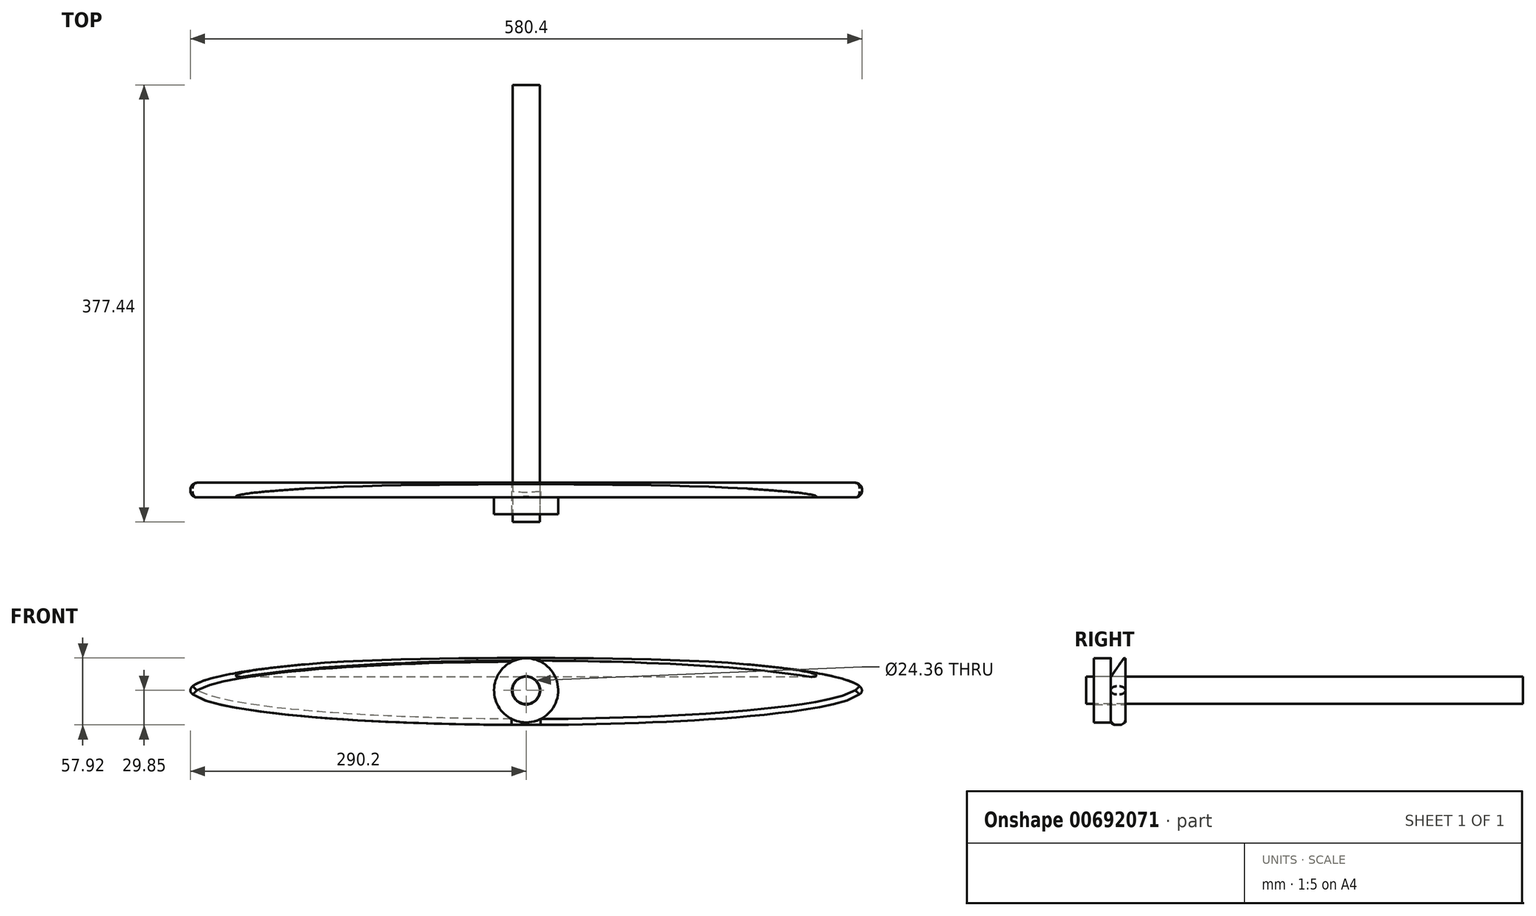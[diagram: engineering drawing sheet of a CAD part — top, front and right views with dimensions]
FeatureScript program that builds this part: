
annotation { "Feature Type Name" : "Feature", "Feature Type Description" : "" }
export const myFeature = defineFeature(function(context is Context, id is Id, definition is map)
    precondition{}
    {
        {
            var Q0;
            Q0=qCreatedBy(makeId("Front.planeOp"),FACE);
            var sketch = newSketch(context, id + "F0", { "sketchPlane" : qUnion([Q0])});
            skEllipse(sketch, "E0", {"center": v(0, 0) * mm, "majorRadius": 290.2 * mm, "minorRadius": 29.85 * mm, "majorAxis": v(1, 0)});
            skCircle(sketch, "E1", {"center": v(0, 0) * mm, "radius": 27.71 * mm});
            skCircle(sketch, "E2", {"center": v(0, 0) * mm, "radius": 12.18 * mm});
            skSolve(sketch);
        }
        {
            var Q0;
            Q0=makeQuery(id+"F0.imprint","IMPRINT",FACE,{"disambiguationData":[TD([[makeQuery(id+"F0.imprint","IMPRINT",EDGE,{"derivedFrom":sQuery(id+"F0.wireOp",EDGE,"E0")}),1.0]])]});
            extrude(context, id + "F1", {"entities" : qUnion([Q0]), "endBound" : BoundingType.SYMMETRIC, "oppositeDirection" : true, "depth" : 12.7 * mm, "offsetDistance" : 25.4 * mm});
        }
        {
            var Q0;
            Q0=makeQuery(id+"F0.imprint","IMPRINT",FACE,{"disambiguationData":[TD([[makeQuery(id+"F0.imprint","IMPRINT",EDGE,{"derivedFrom":sQuery(id+"F0.wireOp",EDGE,"E1")}),1.0]])]});
            extrude(context, id + "F2", {"entities" : qUnion([Q0]), "operationType" : NewBodyOperationType.ADD, "depth" : 20.83 * mm, "offsetDistance" : 25.4 * mm});
        }
        {
            var Q0;
            Q0=makeQuery(id+"F1.opExtrude","CAP_EDGE",EDGE,{"disambiguationData":[OSD([sQuery(id+"F0.wireOp",EDGE,"E0")])],"isStart":true});
            var Q1;
            Q1=makeQuery(id+"F1.opExtrude","CAP_EDGE",EDGE,{"disambiguationData":[OSD([sQuery(id+"F0.wireOp",EDGE,"E0")])],"isStart":false});
            fillet(context, id + "F3", {"entities" : qUnion([Q0, Q1]), "radius" : 5.08 * mm, "tangentPropagation" : true, "allowEdgeOverflow" : false});
        }
        {
            var Q0;
            Q0=makeQuery(id+"F0.imprint","IMPRINT",FACE,{"disambiguationData":[TD([[makeQuery(id+"F0.imprint","IMPRINT",EDGE,{"derivedFrom":sQuery(id+"F0.wireOp",EDGE,"E1")}),1.0]])]});
            extrude(context, id + "F4", {"entities" : qUnion([Q0]), "operationType" : NewBodyOperationType.ADD, "oppositeDirection" : true, "depth" : 6.35 * mm, "offsetDistance" : 25.4 * mm});
        }
        {
            var Q0;
            Q0=qCreatedBy(makeId("Right.planeOp"),FACE);
            var sketch = newSketch(context, id + "F5", { "sketchPlane" : qUnion([Q0])});
            skLineSegment(sketch, "E3", {"start": v(18.47, 47.35) * mm, "end": v(-6.25, 11.6) * mm});
            skLineSegment(sketch, "E4", {"start": v(-6.25, 11.6) * mm, "end": v(-6.25, 33.84) * mm});
            skLineSegment(sketch, "E5", {"start": v(-6.25, 33.84) * mm, "end": v(18.47, 47.35) * mm});
            skSolve(sketch);
        }
        {
            var Q0;
            Q0 = qSketchRegion(id + "F5", true);
            extrude(context, id + "F6", {"entities" : qUnion([Q0]), "operationType" : NewBodyOperationType.REMOVE, "endBound" : BoundingType.SYMMETRIC, "depth" : 772.16 * mm, "offsetDistance" : 25.4 * mm});
        }
        {
            var Q0;
            Q0=sQuery(id+"F0.wireOp",EDGE,"E1");
            extrude(context, id + "F7", {"bodyType" : ToolBodyType.SURFACE, "surfaceEntities" : qUnion([Q0]), "oppositeDirection" : true, "depth" : 5.84 * mm, "offsetDistance" : 25.4 * mm});
        }
        {
            var Q0;
            Q0=qCreatedBy(makeId("Front.planeOp"),FACE);
            var sketch = newSketch(context, id + "F8", { "sketchPlane" : qUnion([Q0])});
            skCircle(sketch, "E6", {"center": v(0, 0) * mm, "radius": 11.77 * mm});
            skSolve(sketch);
        }
        {
            var Q0;
            Q0 = qSketchRegion(id + "F8", true);
            extrude(context, id + "F9", {"entities" : qUnion([Q0]), "endBound" : BoundingType.SYMMETRIC, "oppositeDirection" : true, "depth" : 54.86 * mm, "offsetDistance" : 25.4 * mm});
        }
        {
            var Q0;
            Q0=makeQuery(id+"F9.opExtrude","CAP_FACE",FACE,{"disambiguationData":[OSD([sQuery(id+"F8.wireOp",EDGE,"E6")])],"isStart":false});
            extrude(context, id + "F10", {"entities" : qUnion([Q0]), "operationType" : NewBodyOperationType.ADD, "depth" : 322.58 * mm, "offsetDistance" : 25.4 * mm});
        }
    });
